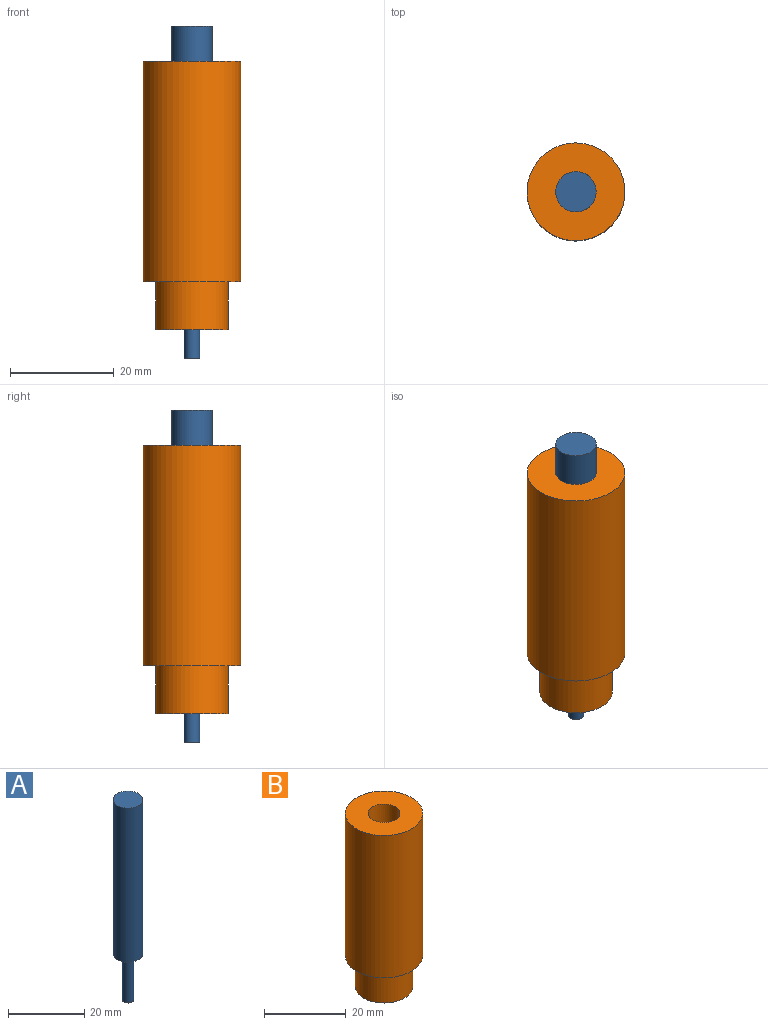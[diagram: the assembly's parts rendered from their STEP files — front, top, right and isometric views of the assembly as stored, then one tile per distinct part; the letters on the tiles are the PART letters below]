
ASSEMBLY  parts=2 mates=1
PART A: 5 faces, bbox 7.8x7.8x64.2 mm
  f0: cylinder r=1.5mm len=14.75mm, axis (0,0,1), area 139mm2, adj f1,f4
  f1: plane 3x3mm, normal (0,0,-1), area 7.1mm2, adj f0
  f2: cylinder r=3.9mm len=49.4mm, axis (0,0,-1), area 1210.5mm2, adj f3,f4
  f3: plane 7.8x7.8mm, normal (0,0,1), area 47.8mm2, adj f2
  f4: plane 7.8x7.8mm, normal (0,0,-1), area 40.7mm2, adj f0,f2
PART B: 8 faces, bbox 18.9x18.9x51.9 mm
  f0: cylinder r=9.45mm len=42.6mm, axis (0,0,-1), area 2529.4mm2, adj f2,f3
  f1: cylinder r=3.9mm len=42.6mm, axis (0,0,-1), area 1043.9mm2, adj f2,f7
  f2: plane 18.9x18.9mm, normal (0,0,1), area 232.8mm2, adj f0,f1
  f3: plane 18.9x18.9mm, normal (0,0,-1), area 126.6mm2, adj f0,f4
  f4: cylinder r=7mm len=14mm, axis (0,0,1), area 406.8mm2, adj f3,f6
  f5: cylinder r=1.5mm len=9.25mm, axis (0,0,1), area 87.2mm2, adj f6,f7
  f6: plane 14x14mm, normal (0,0,-1), area 146.9mm2, adj f4,f5
  f7: plane 7.8x7.8mm, normal (0,0,1), area 40.7mm2, adj f1,f5
PLACE A rot(axis=(0,0,-1),166.3deg) t=(-1.21,12.49,7.96)mm
PLACE B t=(-1.21,12.49,7.96)mm fixed
MATE cylindrical A.f2 <-> B.f1  axis (0,0,-1) through (-1.21,12.49,7.96)mm
